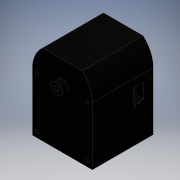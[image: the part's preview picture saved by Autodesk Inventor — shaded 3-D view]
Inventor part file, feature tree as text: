
AUTODESK INVENTOR PART (.ipt)
format: ipt  version: 2016 (Build 200138000, 138)  size: 247,296 bytes
history: native  units: mm
features: extrude x10, sketch x10, other x1
ambient origin geometry x8: Origin, YZ Plane, XZ Plane, XY Plane, X Axis, Y Axis, Z Axis, Center Point
bodies: Body1 (feature_tree)
feature tree (21):
  other  "ソリッド1"
  extrude  "押し出し1"  Depth=32.0mm
  extrude  "押し出し2"  Depth=43.0mm
  extrude  "押し出し3"  Depth=32.5mm TaperAngle=0.0deg
  extrude  "押し出し4"  Depth=9.5mm
  extrude  "押し出し5"  Depth=32.5mm TaperAngle=0.0deg
  extrude  "押し出し6"  Depth=8.5mm
  extrude  "押し出し7"  Depth=13.5mm
  extrude  "押し出し8"  Depth=2.0mm
  extrude  "押し出し9"  Depth=13.5mm
  extrude  "押し出し10"  Depth=2.0mm
  sketch  "スケッチ1"
  sketch  "スケッチ2"
  sketch  "スケッチ3"
  sketch  "スケッチ4"
  sketch  "スケッチ5"
  sketch  "スケッチ6"
  sketch  "スケッチ7"
  sketch  "スケッチ8"
  sketch  "スケッチ9"
  sketch  "スケッチ10"
